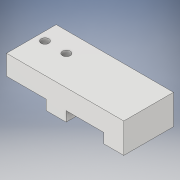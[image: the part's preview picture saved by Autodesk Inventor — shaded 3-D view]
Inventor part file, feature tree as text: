
AUTODESK INVENTOR PART (.ipt)
format: ipt  version: 2019 (Build 230136000, 136)  size: 123,392 bytes
history: native  units: mm
features: extrude x2, sketch x2
ambient origin geometry x8: Origin, YZ Plane, XZ Plane, XY Plane, X Axis, Y Axis, Z Axis, Center Point
bodies: Solid1 (feature_tree)
feature tree (4):
  extrude  "Extrusion1"  Depth=10.0mm
  extrude  "Extrusion2"  Depth=20.0mm
  sketch  "Sketch1"  dims[d0=19.0mm d1=10.0mm]
  sketch  "Sketch2"  dims[d2=10.0mm d3=20.0mm d4=10.0mm d5=5.0mm d6=59.0mm d7=10.0mm d8=25.0mm d9=0.0mm d10=4.0mm d11=4.0mm d12=10.8mm d14=5.0mm d15=10.0mm d16=10.0mm d17=20.0mm d18=0.0mm]
